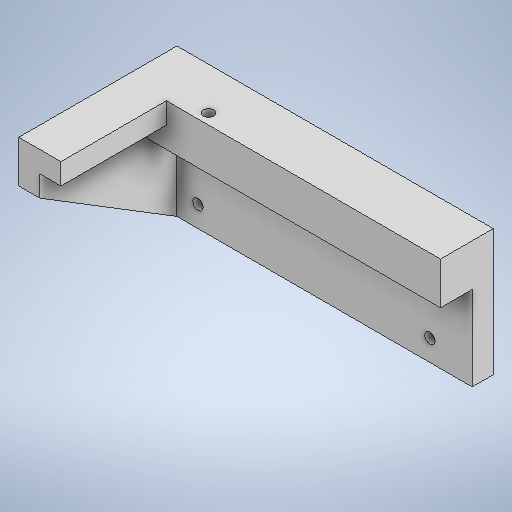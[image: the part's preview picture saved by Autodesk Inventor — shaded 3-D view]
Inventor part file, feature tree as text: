
AUTODESK INVENTOR PART (.ipt)
format: ipt  version: 2025.3 (Build 293356000, 356)  size: 296,448 bytes
history: native  units: mm
features: extrude x6, sketch x5, other x3, projected_geometry x2, mirror x1, hole x1
ambient origin geometry x8: Origin, YZ Plane, XZ Plane, XY Plane, X Axis, Y Axis, Z Axis, Center Point
bodies: Body1 (feature_tree)
feature tree (18):
  other  "솔리드1"
  sketch  "스케치1"
  extrude  "돌출1"  Depth=10.0mm
  extrude  "돌출2"  Depth=300.0mm
  extrude  "돌출3"  Depth=25.0mm TaperAngle=0.0deg
  extrude  "돌출4"  Depth=60.0mm
  other  "작업 평면1"
  mirror  "미러1"
  extrude  "돌출5"  Depth=10.0mm TaperAngle=0.0deg
  hole  "구멍1"  [1 undecoded]
  other  "작업 평면2"
  extrude  "돌출6"  Depth=10.0mm
  sketch  "스케치2"
  projected_geometry  "투영된 루프1"
  sketch  "스케치3"
  sketch  "스케치4"
  sketch  "스케치5"
  projected_geometry  "투영된 루프2"
note: 1 required parameter value undecoded (feature->parameter linkage not recoverable at this tier; creation-order binding heuristic only, values carry confidence <= 0.55)
